# Revit family: Декстер
name_source: partatom
category: Осветительные приборы
units: mm (PartAtom-declared; Revit-internal decimal feet)

## family parameters
Всегда вертикально = Да
Источник света = Да
На основе рабочей плоскости = Нет
Общий = Нет
При загрузке вырезать с полостями = Нет
Размер круглого соединителя = Использовать диаметр
Тип детали = Нормальный
Точка расчета площади = Нет

## types (1)
- ДТУ147с1 Светодиодный светильник Декстер ДТУ-147-AF-40Вт-4,0
    ADSK_URL страницы изделия = https://www.allfresco.ru
    ADSK_Артикул = ДТУ147с1
    ADSK_Единица измерения = шт.
    ADSK_Завод-изготовитель = ALFRESCO
    ADSK_Количество фаз = 2
    ADSK_Количество фаз числовое = 0
    ADSK_Коэффициент мощности = 0
    ADSK_Масса = 55
    ADSK_Масса_Текст = 55
    ADSK_Модель = Декстер ДТУ-147-AF
    ADSK_Наименование = ДТУ147с1 Светодиодный светильник Декстер ДТУ-147-AF-40Вт-4.0
    ADSK_Напряжение = 220 В
    ADSK_Номинальная мощность = 40 Вт
    ADSK_Полная мощность = 0 В·А
    ADSK_Размер_Высота = 4000 мм
    ADSK_Ток = 0 А
    ADSK_Фактическая мощность = 38 Вт
    ADSK_Энергоэффективность = 110 лм/Вт
    D_столб_низ = 133 мм
    D_фланец = 260 мм
    D_фланец_отверстиеРазмер = 20 мм
    D_фланец_отверстия = 200 мм
    H_дверка = 1000 мм
    H_конечной точки = 1500 мм
    H_столб_низ = 1305 мм
    H_фланец = 14 мм
    IP Class = IP 67
    L_отступ до конечной точки = 1500 мм
    L_отступ до центра = 1000 мм
    Блок аварийного питания = Нет
    Класс защиты = 1
    Класс пожароопасности = F (светильники предназначены для установки непосредственно на поверхность из нормально воспламеняемых материалов)
    Климатическая зона = УХЛ1
    Короб_Диаметр = 20 мм
    Корпус светильника = Серый металл
    Материал рассеивателя = Светотехнический ПК
    Область использования = Парки, скверы, общественные пространства, городская инфраструктура
    Полная установленная мощность = 0 В·А
    Рассеиватель = Белый_светодиод
    Светофильтр = 16777215
    Смещение цветовой температуры при затухании лампы = <Нет>
    Таблица выбора = Таблица параметров светильников_par2
    Температура эксплуатации = -40 +50
    Тип ИС = LED-модуль
    Тип КСС = тип ШБ (широкая боковая)
    Тип ПРА = -
    Тип продукции = LED-светильник
    Угол наклона = 90.00°
    Файл фотометрической сетки = DTU-147-AF Dexter 40W 146x60.ies
    Цветоывая температура = 2700-5500

## geometry (parser evidence)
native form markers: Blend x2
no freeform markers — native parametric forms only
